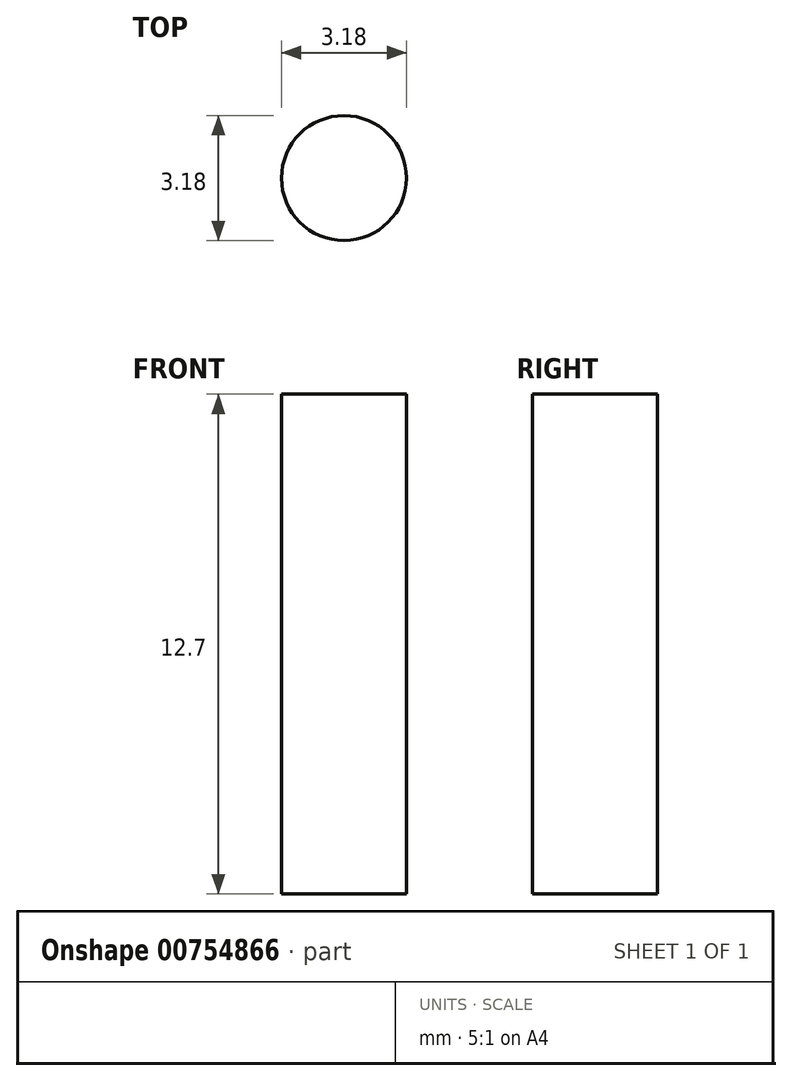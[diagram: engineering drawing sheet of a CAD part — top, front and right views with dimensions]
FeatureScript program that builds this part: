
annotation { "Feature Type Name" : "Feature", "Feature Type Description" : "" }
export const myFeature = defineFeature(function(context is Context, id is Id, definition is map)
    precondition{}
    {
        {
            var Q0;
            Q0=qCreatedBy(makeId("Top.planeOp"),FACE);
            var sketch = newSketch(context, id + "F0", { "sketchPlane" : qUnion([Q0])});
            skCircle(sketch, "E0", {"center": v(-9.14, 0) * mm, "radius": 1.59 * mm});
            skSolve(sketch);
        }
        {
            var Q0;
            Q0 = qSketchRegion(id + "F0", true);
            extrude(context, id + "F1", {"entities" : qUnion([Q0]), "depth" : 12.7 * mm, "offsetDistance" : 25.4 * mm});
        }
    });
